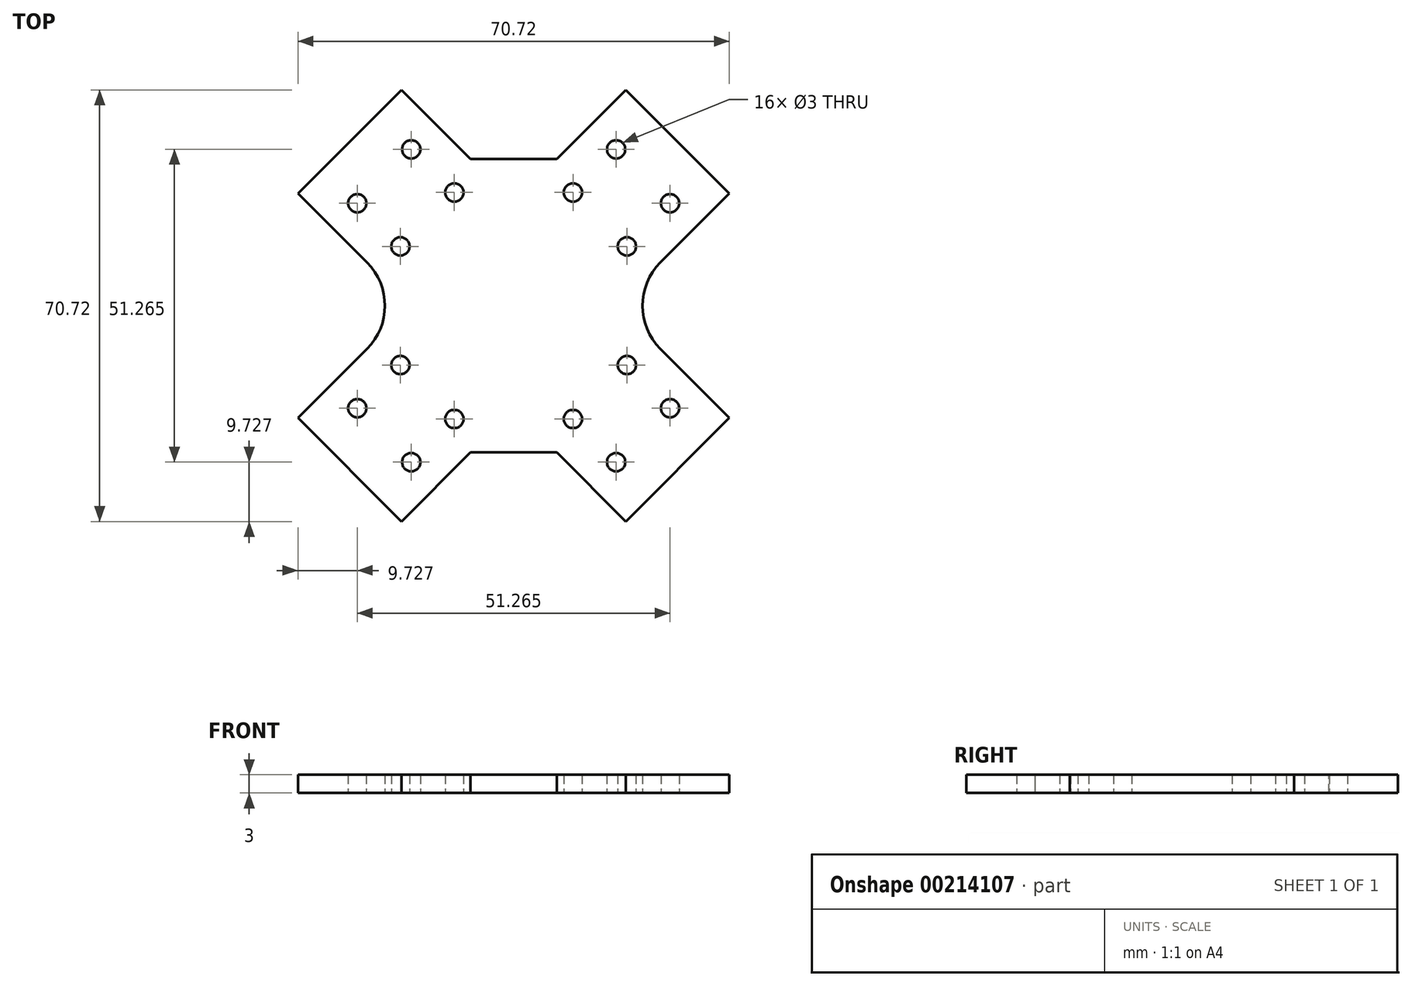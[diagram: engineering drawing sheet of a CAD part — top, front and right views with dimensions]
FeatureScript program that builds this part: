
annotation { "Feature Type Name" : "Feature", "Feature Type Description" : "" }
export const myFeature = defineFeature(function(context is Context, id is Id, definition is map)
    precondition{}
    {
        {
            var Q0;
            Q0=qCreatedBy(makeId("Top.planeOp"),FACE);
            var sketch = newSketch(context, id + "F0", { "sketchPlane" : qUnion([Q0])});
            skLineSegment(sketch, "E0", {"start": v(-53.03, 53.03) * mm, "end": v(53.03, -53.03) * mm, "construction": true});
            skLineSegment(sketch, "E1", {"start": v(-53.03, -53.03) * mm, "end": v(53.03, 53.03) * mm, "construction": true});
            skCircle(sketch, "E2", {"center": v(9.72, 18.56) * mm, "radius": 1.5 * mm});
            skCircle(sketch, "E3", {"center": v(16.8, 25.63) * mm, "radius": 1.5 * mm});
            skCircle(sketch, "E4", {"center": v(25.63, 16.8) * mm, "radius": 1.5 * mm});
            skCircle(sketch, "E5", {"center": v(18.56, 9.72) * mm, "radius": 1.5 * mm});
            skLineSegment(sketch, "E6", {"start": v(9.72, 18.56) * mm, "end": v(18.56, 9.72) * mm, "construction": true});
            skLineSegment(sketch, "E7", {"start": v(16.8, 25.63) * mm, "end": v(25.63, 16.8) * mm, "construction": true});
            skCircle(sketch, "E8.1.0", {"center": v(16.8, -25.63) * mm, "radius": 1.5 * mm});
            skCircle(sketch, "E8.1.1", {"center": v(25.63, -16.8) * mm, "radius": 1.5 * mm});
            skCircle(sketch, "E8.1.2", {"center": v(18.56, -9.72) * mm, "radius": 1.5 * mm});
            skCircle(sketch, "E8.1.3", {"center": v(9.72, -18.56) * mm, "radius": 1.5 * mm});
            skCircle(sketch, "E8.2.0", {"center": v(-25.63, -16.8) * mm, "radius": 1.5 * mm});
            skCircle(sketch, "E8.2.1", {"center": v(-16.8, -25.63) * mm, "radius": 1.5 * mm});
            skCircle(sketch, "E8.2.2", {"center": v(-9.72, -18.56) * mm, "radius": 1.5 * mm});
            skCircle(sketch, "E8.2.3", {"center": v(-18.56, -9.72) * mm, "radius": 1.5 * mm});
            skCircle(sketch, "E8.3.0", {"center": v(-16.8, 25.63) * mm, "radius": 1.5 * mm});
            skCircle(sketch, "E8.3.1", {"center": v(-25.63, 16.8) * mm, "radius": 1.5 * mm});
            skCircle(sketch, "E8.3.2", {"center": v(-18.56, 9.72) * mm, "radius": 1.5 * mm});
            skCircle(sketch, "E8.3.3", {"center": v(-9.72, 18.56) * mm, "radius": 1.5 * mm});
            skPoint(sketch, "E8.center", {"position": v(0, 0) * mm});
            skLineSegment(sketch, "E8.anchor1", {"start": v(0, 0) * mm, "end": v(25.63, 16.8) * mm, "construction": true});
            skLineSegment(sketch, "E8.anchor2", {"start": v(0, 0) * mm, "end": v(-16.8, 25.63) * mm, "construction": true});
            skLineSegment(sketch, "E9", {"start": v(-16.97, 0) * mm, "end": v(-35.36, 18.38) * mm});
            skLineSegment(sketch, "E10", {"start": v(-35.36, 18.38) * mm, "end": v(-18.38, 35.36) * mm});
            skLineSegment(sketch, "E11", {"start": v(-18.38, 35.36) * mm, "end": v(0, 16.97) * mm});
            skLineSegment(sketch, "E12", {"start": v(0, 16.97) * mm, "end": v(18.38, 35.36) * mm});
            skLineSegment(sketch, "E13", {"start": v(18.38, 35.36) * mm, "end": v(35.36, 18.38) * mm});
            skLineSegment(sketch, "E14", {"start": v(35.36, 18.38) * mm, "end": v(16.97, 0) * mm});
            skLineSegment(sketch, "E15.MirrorCS", {"start": v(35.36, -18.38) * mm, "end": v(16.97, 0) * mm});
            skLineSegment(sketch, "E16.MirrorCS", {"start": v(18.38, -35.36) * mm, "end": v(35.36, -18.38) * mm});
            skLineSegment(sketch, "E17.MirrorCS", {"start": v(0, -16.97) * mm, "end": v(18.38, -35.36) * mm});
            skLineSegment(sketch, "E18.MirrorCS", {"start": v(-18.38, -35.36) * mm, "end": v(0, -16.97) * mm});
            skLineSegment(sketch, "E19.MirrorCS", {"start": v(-35.36, -18.38) * mm, "end": v(-18.38, -35.36) * mm});
            skLineSegment(sketch, "E20.MirrorCS", {"start": v(-16.97, 0) * mm, "end": v(-35.36, -18.38) * mm});
            skSolve(sketch);
        }
        {
            var Q0;
            Q0=makeQuery(id+"F0.imprint","IMPRINT",FACE,{"disambiguationData":[TD([[makeQuery(id+"F0.imprint","IMPRINT",EDGE,{"derivedFrom":sQuery(id+"F0.wireOp",EDGE,"E2")}),-1.0]])]});
            extrude(context, id + "F1", {"entities" : qUnion([Q0]), "depth" : 3 * mm});
        }
        {
            var Q0;
            Q0=makeQuery(id+"F1.opExtrude","SWEPT_EDGE",EDGE,{"disambiguationData":[OSD([sQuery(id+"F0.wireOp",EDGE,"E9"),sQuery(id+"F0.wireOp",EDGE,"E20.MirrorCS")])]});
            var Q1;
            Q1=makeQuery(id+"F1.opExtrude","SWEPT_EDGE",EDGE,{"disambiguationData":[OSD([sQuery(id+"F0.wireOp",EDGE,"E14"),sQuery(id+"F0.wireOp",EDGE,"E15.MirrorCS")])]});
            fillet(context, id + "F2", {"entities" : qUnion([Q0, Q1]), "radius" : 10 * mm, "tangentPropagation" : true, "allowEdgeOverflow" : false});
        }
        {
            var Q0;
            Q0=makeQuery(id+"F1.opExtrude","SWEPT_EDGE",EDGE,{"disambiguationData":[OSD([sQuery(id+"F0.wireOp",EDGE,"E17.MirrorCS"),sQuery(id+"F0.wireOp",EDGE,"E18.MirrorCS")])]});
            var Q1;
            Q1=makeQuery(id+"F1.opExtrude","SWEPT_EDGE",EDGE,{"disambiguationData":[OSD([sQuery(id+"F0.wireOp",EDGE,"E11"),sQuery(id+"F0.wireOp",EDGE,"E12")])]});
            chamfer(context, id + "F3", {"entities" : qUnion([Q0, Q1]), "width" : 10 * mm, "tangentPropagation" : true});
        }
    });
